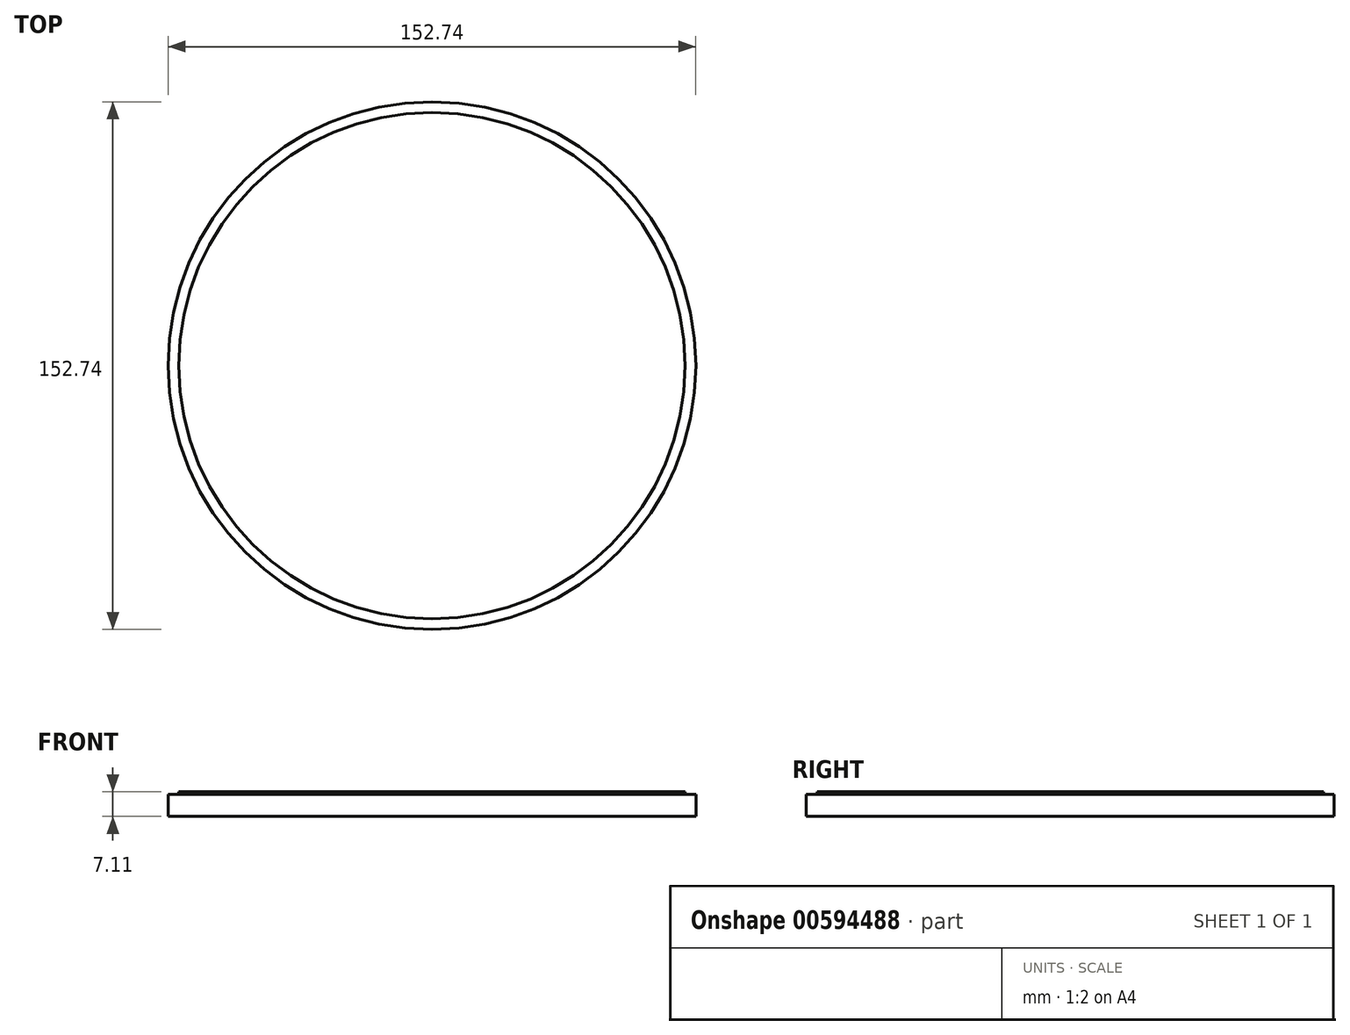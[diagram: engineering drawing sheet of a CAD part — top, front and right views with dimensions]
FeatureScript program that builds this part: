
annotation { "Feature Type Name" : "Feature", "Feature Type Description" : "" }
export const myFeature = defineFeature(function(context is Context, id is Id, definition is map)
    precondition{}
    {
        {
            var Q0;
            Q0=qCreatedBy(makeId("Top.planeOp"),FACE);
            var sketch = newSketch(context, id + "F0", { "sketchPlane" : qUnion([Q0])});
            skCircle(sketch, "E0", {"center": v(0, 0) * mm, "radius": 76.37 * mm});
            skCircle(sketch, "E1", {"center": v(0, 0) * mm, "radius": 73.28 * mm});
            skCircle(sketch, "E2", {"center": v(0, 0) * mm, "radius": 70.43 * mm});
            skSolve(sketch);
        }
        {
            var Q0;
            Q0 = qSketchRegion(id + "F0", true);
            extrude(context, id + "F1", {"entities" : qUnion([Q0]), "depth" : 6.35 * mm, "offsetDistance" : 25.4 * mm});
        }
        {
            var Q0;
            Q0=makeQuery(id+"F0.imprint","IMPRINT",FACE,{"disambiguationData":[TD([[makeQuery(id+"F0.imprint","IMPRINT",EDGE,{"derivedFrom":sQuery(id+"F0.wireOp",EDGE,"E1")}),1.0]])]});
            var Q1;
            Q1=makeQuery(id+"F0.imprint","IMPRINT",FACE,{"disambiguationData":[TD([[makeQuery(id+"F0.imprint","IMPRINT",EDGE,{"derivedFrom":sQuery(id+"F0.wireOp",EDGE,"E2")}),1.0]])]});
            extrude(context, id + "F2", {"entities" : qUnion([Q0, Q1]), "operationType" : NewBodyOperationType.ADD, "depth" : 7.11 * mm, "offsetDistance" : 25.4 * mm});
        }
    });
